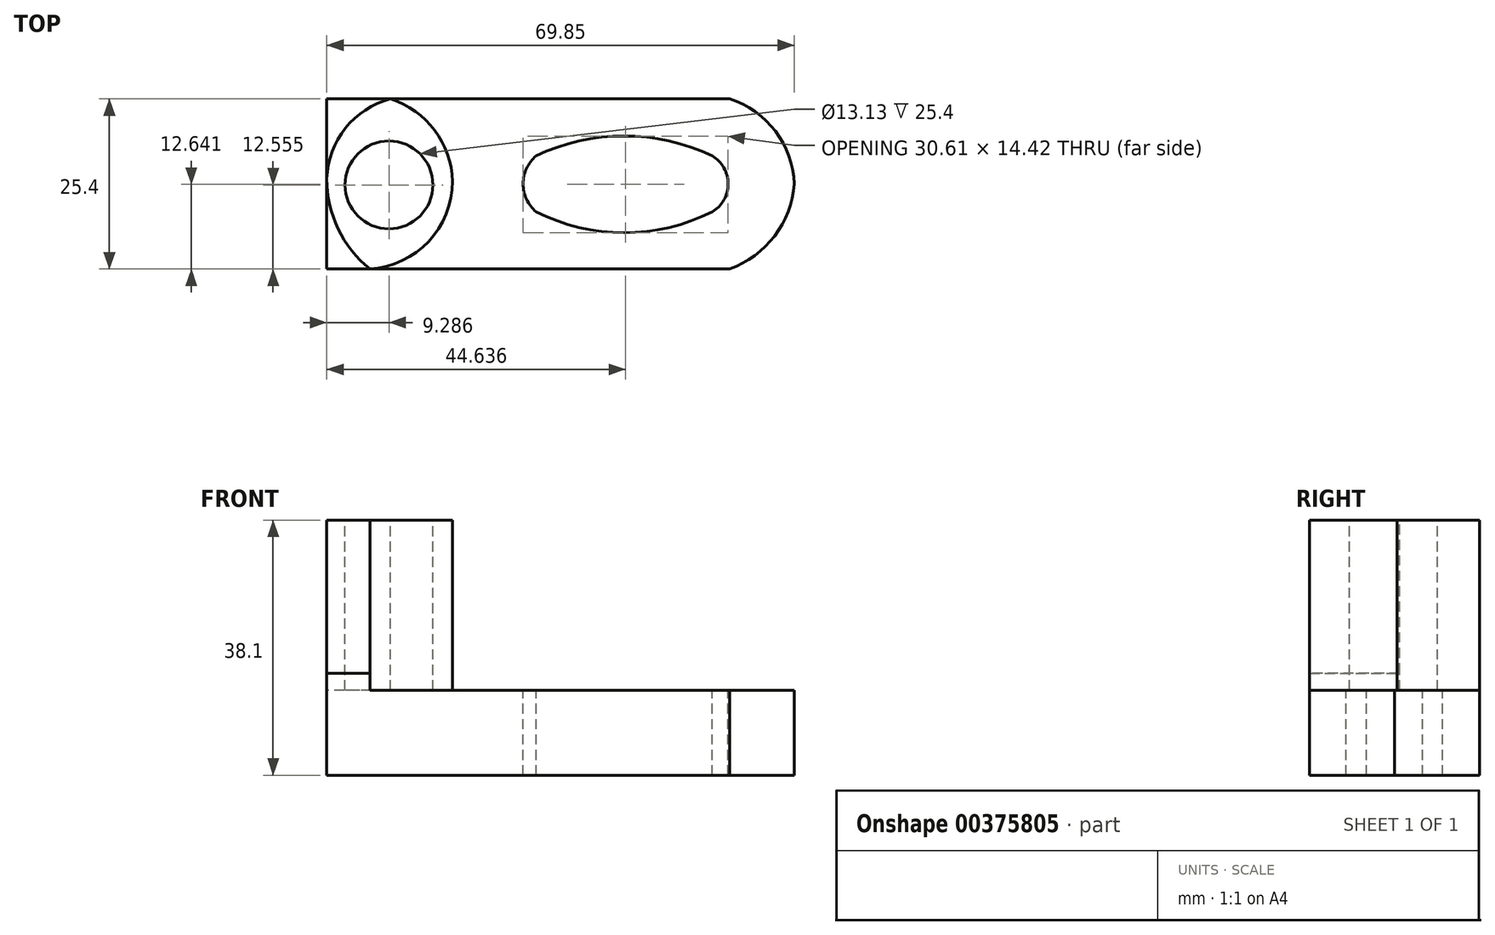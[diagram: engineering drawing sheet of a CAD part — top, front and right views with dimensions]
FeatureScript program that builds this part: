
annotation { "Feature Type Name" : "Feature", "Feature Type Description" : "" }
export const myFeature = defineFeature(function(context is Context, id is Id, definition is map)
    precondition{}
    {
        {
            var Q0;
            Q0=qCreatedBy(makeId("Front.planeOp"),FACE);
            var sketch = newSketch(context, id + "F0", { "sketchPlane" : qUnion([Q0])});
            skLineSegment(sketch, "E0", {"start": v(0, 0) * mm, "end": v(69.85, 0) * mm});
            skLineSegment(sketch, "E1", {"start": v(69.85, 0) * mm, "end": v(69.85, 12.7) * mm});
            skLineSegment(sketch, "E2", {"start": v(69.85, 12.7) * mm, "end": v(19.05, 12.7) * mm});
            skLineSegment(sketch, "E3", {"start": v(19.05, 12.7) * mm, "end": v(19.05, 38.1) * mm});
            skLineSegment(sketch, "E4", {"start": v(19.05, 38.1) * mm, "end": v(0, 38.1) * mm});
            skLineSegment(sketch, "E5", {"start": v(0, 38.1) * mm, "end": v(0, 0) * mm});
            skSolve(sketch);
        }
        {
            var Q0;
            Q0=makeQuery(id+"F0.imprint","IMPRINT",FACE,{"disambiguationData":[TD([[makeQuery(id+"F0.imprint","IMPRINT",EDGE,{"derivedFrom":sQuery(id+"F0.wireOp",EDGE,"E0")}),1.0]])]});
            extrude(context, id + "F1", {"entities" : qUnion([Q0]), "depth" : 25.4 * mm});
        }
        {
            var Q0;
            Q0=makeQuery(id+"F1.opExtrude","SWEPT_FACE",FACE,{"disambiguationData":[OSD([sQuery(id+"F0.wireOp",EDGE,"E2")])]});
            var sketch = newSketch(context, id + "F2", { "sketchPlane" : qUnion([Q0])});
            skArc(sketch, "E6", {"start": v(60.19, -25.4) * mm, "mid": v(66.88, -20.47) * mm, "end": v(69.85, -12.7) * mm});
            skArc(sketch, "E7", {"start": v(69.85, -12.7) * mm, "mid": v(67.02, -4.83) * mm, "end": v(60.19, 0) * mm});
            skSolve(sketch);
        }
        {
            var Q0;
            Q0 = qSketchRegion(id + "F2", true);
            var Q1;
            {var subQ0=sQuery(id+"F2.wireOp",EDGE,"E7");Q1=makeQuery(id+"F2.imprint","IMPRINT",FACE,{"disambiguationData":[TD([[makeQuery(id+"F2.imprint","IMPRINT",EDGE,{"derivedFrom":subQ0}),-1.0]])]});}
            var Q2;
            {var subQ0=sQuery(id+"F2.wireOp",EDGE,"E6");Q2=makeQuery(id+"F2.imprint","IMPRINT",FACE,{"disambiguationData":[TD([[makeQuery(id+"F2.imprint","IMPRINT",EDGE,{"derivedFrom":subQ0}),-1.0]])]});}
            extrude(context, id + "F3", {"entities" : qUnion([Q0, Q1, Q2]), "operationType" : NewBodyOperationType.REMOVE, "oppositeDirection" : true, "depth" : 25.4 * mm});
        }
        {
            var Q0;
            Q0=makeQuery(id+"F1.opExtrude","SWEPT_FACE",FACE,{"disambiguationData":[OSD([sQuery(id+"F0.wireOp",EDGE,"E2")])]});
            var sketch = newSketch(context, id + "F4", { "sketchPlane" : qUnion([Q0])});
            skArc(sketch, "E8", {"start": v(31.26, -8.51) * mm, "mid": v(29.33, -12.7) * mm, "end": v(31.26, -16.87) * mm});
            skArc(sketch, "E9", {"start": v(57.57, -8.51) * mm, "mid": v(44.42, -5.55) * mm, "end": v(31.26, -8.51) * mm});
            skArc(sketch, "E10", {"start": v(57.57, -16.87) * mm, "mid": v(59.94, -12.7) * mm, "end": v(57.57, -8.51) * mm});
            skArc(sketch, "E11", {"start": v(31.26, -16.87) * mm, "mid": v(44.42, -19.97) * mm, "end": v(57.57, -16.87) * mm});
            skSolve(sketch);
        }
        {
            var Q0;
            Q0=makeQuery(id+"F4.imprint","IMPRINT",FACE,{"disambiguationData":[TD([[makeQuery(id+"F4.imprint","IMPRINT",EDGE,{"derivedFrom":sQuery(id+"F4.wireOp",EDGE,"E8")}),1.0]])]});
            extrude(context, id + "F5", {"entities" : qUnion([Q0]), "operationType" : NewBodyOperationType.REMOVE, "oppositeDirection" : true, "depth" : 25.4 * mm});
        }
        {
            var Q0;
            Q0=makeQuery(id+"F1.opExtrude","SWEPT_FACE",FACE,{"disambiguationData":[OSD([sQuery(id+"F0.wireOp",EDGE,"E4")])]});
            var sketch = newSketch(context, id + "F6", { "sketchPlane" : qUnion([Q0])});
            skCircle(sketch, "E12", {"center": v(9.29, -12.84) * mm, "radius": 6.57 * mm});
            skSolve(sketch);
        }
        {
            var Q0;
            Q0=makeQuery(id+"F6.imprint","IMPRINT",FACE,{"disambiguationData":[TD([[makeQuery(id+"F6.imprint","IMPRINT",EDGE,{"derivedFrom":sQuery(id+"F6.wireOp",EDGE,"E12")}),1.0]])]});
            extrude(context, id + "F7", {"entities" : qUnion([Q0]), "operationType" : NewBodyOperationType.REMOVE, "oppositeDirection" : true, "depth" : 25.4 * mm});
        }
        {
            var Q0;
            Q0=makeQuery(id+"F1.opExtrude","SWEPT_FACE",FACE,{"disambiguationData":[OSD([sQuery(id+"F0.wireOp",EDGE,"E4")])]});
            var sketch = newSketch(context, id + "F8", { "sketchPlane" : qUnion([Q0])});
            skArc(sketch, "E13", {"start": v(9.53, -25.4) * mm, "mid": v(18.79, -12.7) * mm, "end": v(9.53, 0) * mm});
            skSolve(sketch);
        }
        {
            var Q0;
            Q0 = qSketchRegion(id + "F8", true);
            var Q1;
            {var subQ0=sQuery(id+"F8.wireOp",EDGE,"E13");Q1=makeQuery(id+"F8.imprint","IMPRINT",FACE,{"disambiguationData":[TD([[makeQuery(id+"F8.imprint","IMPRINT",EDGE,{"derivedFrom":subQ0}),-1.0]])]});}
            extrude(context, id + "F9", {"entities" : qUnion([Q0, Q1]), "operationType" : NewBodyOperationType.REMOVE, "oppositeDirection" : true, "depth" : 25.4 * mm});
        }
        {
            var Q0;
            Q0=makeQuery(id+"F1.opExtrude","SWEPT_FACE",FACE,{"disambiguationData":[OSD([sQuery(id+"F0.wireOp",EDGE,"E4")])]});
            var sketch = newSketch(context, id + "F10", { "sketchPlane" : qUnion([Q0])});
            skArc(sketch, "E14", {"start": v(9.53, 0) * mm, "mid": v(2.54, -4.68) * mm, "end": v(0, -12.7) * mm});
            skArc(sketch, "E15", {"start": v(4.76, -25.4) * mm, "mid": v(14.6, -21.88) * mm, "end": v(18.78, -12.32) * mm});
            skSolve(sketch);
        }
        {
            var Q0;
            Q0 = qSketchRegion(id + "F10", true);
            var Q1;
            {var subQ1=sQuery(id+"F0.wireOp",EDGE,"E4");var subQ2=makeQuery(id+"F1.opExtrude","CAP_EDGE",EDGE,{"disambiguationData":[OSD([subQ1])],"isStart":true});Q1=makeQuery(id+"F10.imprint","IMPRINT",FACE,{"disambiguationData":[TD([[makeQuery(id+"F10.imprint","IMPRINT",EDGE,{"derivedFrom":subQ2}),1.0]])]});}
            var Q2;
            {var subQ0=sQuery(id+"F10.wireOp",EDGE,"E15");var subQ1=makeQuery(id+"F9.boolean.opBoolean","COPY",EDGE,{"derivedFrom":makeQuery(id+"F9.opExtrude","CAP_EDGE",EDGE,{"disambiguationData":[OSD([sQuery(id+"F8.wireOp",EDGE,"E13")])],"isStart":true})});var subQ2=makeQuery(id+"F10.imprint","INTERSECT",VERTEX,{"derivedFrom":[subQ1,subQ0]});Q2=makeQuery(id+"F10.imprint","IMPRINT",FACE,{"disambiguationData":[TD([[makeQuery(id+"F10.imprint","IMPRINT",EDGE,{"disambiguationData":[TD([[subQ2,1.0]])],"derivedFrom":subQ0}),-1.0]])]});}
            extrude(context, id + "F11", {"entities" : qUnion([Q0, Q1, Q2]), "operationType" : NewBodyOperationType.REMOVE, "oppositeDirection" : true, "depth" : 25.4 * mm});
        }
        {
            var Q0;
            Q0=makeQuery(id+"F1.opExtrude","SWEPT_FACE",FACE,{"disambiguationData":[OSD([sQuery(id+"F0.wireOp",EDGE,"E4")])]});
            var sketch = newSketch(context, id + "F12", { "sketchPlane" : qUnion([Q0])});
            skArc(sketch, "E16", {"start": v(0, -11.94) * mm, "mid": v(1.7, -19.4) * mm, "end": v(6.43, -25.4) * mm});
            skSolve(sketch);
        }
        {
            var Q0;
            Q0=makeQuery(id+"F12.imprint","IMPRINT",FACE,{"disambiguationData":[TD([[makeQuery(id+"F12.imprint","IMPRINT",EDGE,{"derivedFrom":sQuery(id+"F12.wireOp",EDGE,"E16")}),-1.0]])]});
            extrude(context, id + "F13", {"entities" : qUnion([Q0]), "operationType" : NewBodyOperationType.REMOVE, "oppositeDirection" : true, "depth" : 22.86 * mm});
        }
    });
